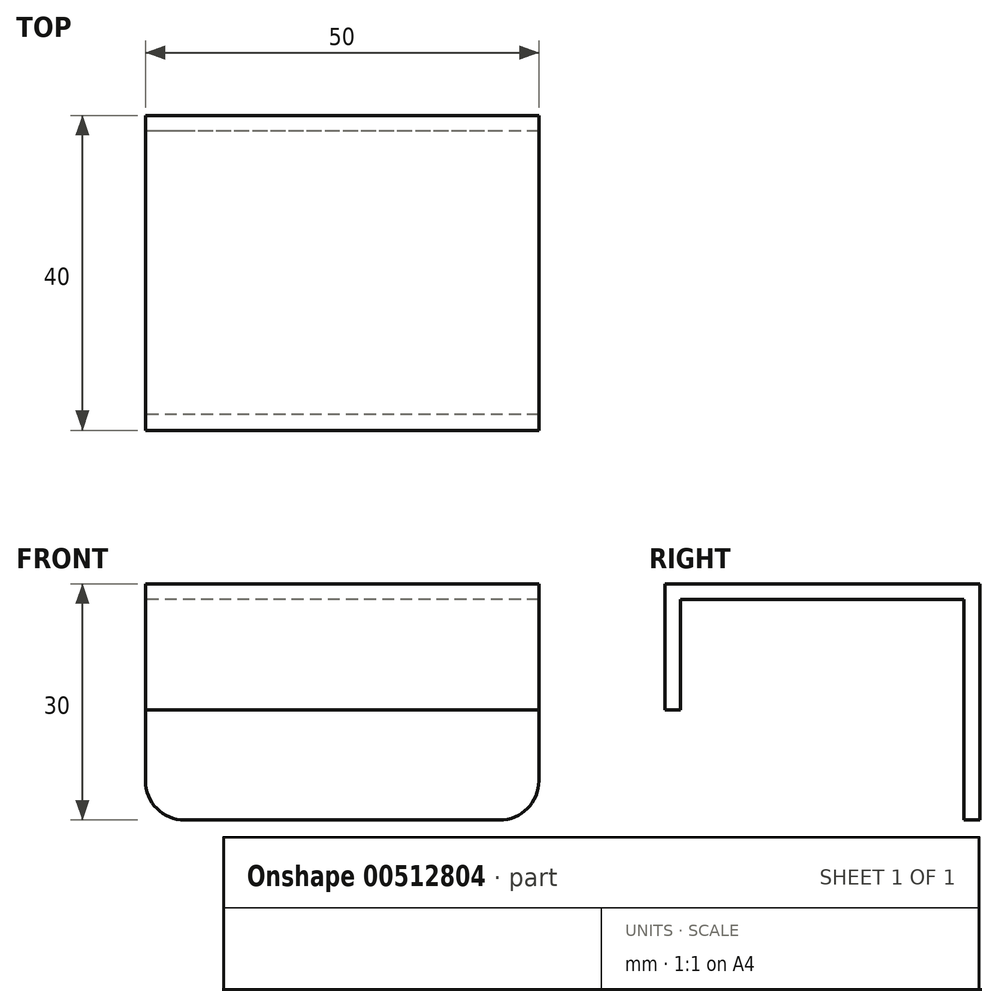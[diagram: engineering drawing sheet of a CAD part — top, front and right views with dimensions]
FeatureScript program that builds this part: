
annotation { "Feature Type Name" : "Feature", "Feature Type Description" : "" }
export const myFeature = defineFeature(function(context is Context, id is Id, definition is map)
    precondition{}
    {
        {
            var Q0;
            Q0=qCreatedBy(makeId("Right.planeOp"),FACE);
            var sketch = newSketch(context, id + "F0", { "sketchPlane" : qUnion([Q0])});
            skLineSegment(sketch, "E0", {"start": v(0, 0) * mm, "end": v(0, 14) * mm});
            skLineSegment(sketch, "E1", {"start": v(0, 14) * mm, "end": v(36, 14) * mm});
            skLineSegment(sketch, "E2", {"start": v(36, 14) * mm, "end": v(36, 16) * mm});
            skLineSegment(sketch, "E3", {"start": v(36, 16) * mm, "end": v(-2, 16) * mm});
            skLineSegment(sketch, "E4", {"start": v(-2, 16) * mm, "end": v(-2, 0) * mm});
            skLineSegment(sketch, "E5", {"start": v(36, 14) * mm, "end": v(36, -14) * mm});
            skLineSegment(sketch, "E6", {"start": v(36, -14) * mm, "end": v(38, -14) * mm});
            skLineSegment(sketch, "E7", {"start": v(38, -14) * mm, "end": v(38, 16) * mm});
            skLineSegment(sketch, "E8", {"start": v(38, 16) * mm, "end": v(36, 16) * mm});
            skLineSegment(sketch, "E9", {"start": v(-2, 0) * mm, "end": v(0, 0) * mm});
            skSolve(sketch);
        }
        {
            var Q0;
            Q0 = qSketchRegion(id + "F0", true);
            extrude(context, id + "F1", {"entities" : qUnion([Q0]), "depth" : 50 * mm});
        }
        {
            var Q0;
            Q0=makeQuery(id+"F1.opExtrude","CAP_EDGE",EDGE,{"disambiguationData":[OSD([sQuery(id+"F0.wireOp",EDGE,"E6")])],"isStart":false});
            var Q1;
            Q1=makeQuery(id+"F1.opExtrude","CAP_EDGE",EDGE,{"disambiguationData":[OSD([sQuery(id+"F0.wireOp",EDGE,"E6")])],"isStart":true});
            fillet(context, id + "F2", {"entities" : qUnion([Q0, Q1]), "radius" : 5 * mm, "tangentPropagation" : true, "allowEdgeOverflow" : false});
        }
    });
